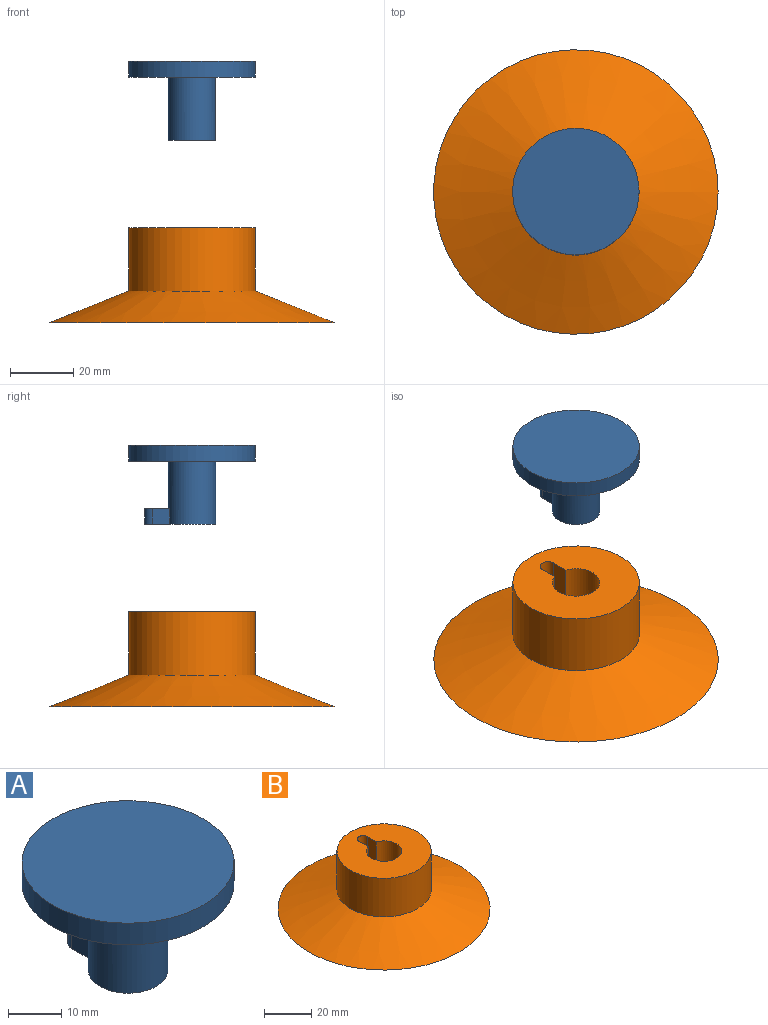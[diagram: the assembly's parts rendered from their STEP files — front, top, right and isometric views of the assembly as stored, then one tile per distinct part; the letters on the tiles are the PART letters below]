
ASSEMBLY  parts=2 mates=1
PART A: 9 faces, bbox 40x40x25 mm
  f0: cylinder r=7.5mm len=20mm, axis (0,0,1), area 917mm2, adj f3,f4,f5,f6,f7
  f1: cylinder r=20mm len=40mm, axis (0,0,1), area 628.3mm2, adj f2,f3
  f2: plane 40x40mm, normal (0,0,1), area 1256.6mm2, adj f1
  f3: plane 40x40mm, normal (0,0,-1), area 1079.9mm2, adj f0,f1
  f4: plane 22.5x15mm, normal (0,0,-1), area 212.2mm2, adj f0,f5,f6,f8
  f5: plane 5.43x5mm, normal (-1,0,0), area 27.1mm2, adj f0,f4,f7,f8
  f6: plane 5.43x5mm, normal (1,0,0), area 27.1mm2, adj f0,f4,f7,f8
  f7: plane 7.93x5mm, normal (0,0,1), area 35.5mm2, adj f0,f5,f6,f8
  f8: cylinder r=2.5mm len=5mm, axis (0,0,1), area 39.3mm2, adj f4,f5,f6,f7
PART B: 13 faces, bbox 90x90x30 mm
  f0: cylinder r=7.5mm len=20mm, axis (0,0,-1), area 794.3mm2, adj f1,f3,f4,f6,f7,f8,f10
  f1: plane 40x40mm, normal (0,0,1), area 1044.4mm2, adj f0,f2,f3,f4,f9
  f2: cylinder r=20mm len=40mm, axis (0,0,-1), area 2513.3mm2, adj f1,f12
  f3: plane 15x5.43mm, normal (-1,0,0), area 81.4mm2, adj f0,f1,f6,f9
  f4: plane 15x5.43mm, normal (1,0,0), area 81.4mm2, adj f0,f1,f6,f9
  f5: cylinder r=16mm len=21.34mm, axis (0,0,-1), area 152.9mm2, adj f6,f7,f8,f10
  f6: plane 21.34x16mm, normal (0,0,-1), area 155.4mm2, adj f0,f3,f4,f5,f7,f8,f9
  f7: plane 8.5x5mm, normal (0,1,0), area 42.5mm2, adj f0,f5,f6,f10
  f8: plane 8.01x5mm, normal (-0.94,0.33,0), area 42.5mm2, adj f0,f5,f6,f10
  f9: cylinder r=2.5mm len=15mm, axis (0,0,1), area 117.8mm2, adj f1,f3,f4,f6
  f10: plane 23.5x23.5mm, normal (0,0,1), area 367.6mm2, adj f0,f5,f7,f8
  f11: plane 90x90mm, normal (0,0,-1), area 6361.7mm2, adj f12
  f12: cone r=45mm half-angle=68.2deg, axis (0,0,-1), area 5498.3mm2, adj f2,f11
PLACE A t=(-117.29,-151.03,107.64)mm
PLACE B rot(axis=(0.93,-0.27,0.23),0deg) t=(-117.29,-151.03,39.96)mm
MATE slider B.f1 <-> A.f7  axis (0,0,1) through (-119.79,-143.96,59.96)mm
